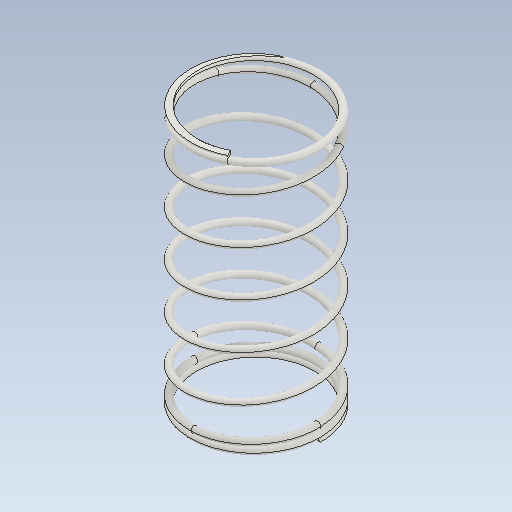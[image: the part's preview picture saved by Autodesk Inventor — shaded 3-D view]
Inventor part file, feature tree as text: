
AUTODESK INVENTOR PART (.ipt)
format: ipt  version: 2020 (Build 240168000, 168)  size: 788,480 bytes
history: native  units: mm
features: other x67, extrude x8, helix x5, sketch x3, sweep x2, plane x1
ambient origin geometry x8: Origin, YZ Plane, XZ Plane, XY Plane, X Axis, Y Axis, Z Axis, Center Point
bodies: Solid1 (feature_tree)
feature tree (86):
  other  "Main Coil Path(Right)"
  other  "Section Work Plane(Right)"
  other  "Start Work Plane(Right)"
  other  "End Work Plane(Right)"
  other  "End Cut Work Plane(Right)"
  other  "Start Cut Work Plane(Right)"
  other  "Plain Ends Cut Work Plane 1(Right)"
  other  "Plain Ends Cut Work Plane 2(Right)"
  sweep  "Main Coil Feature(R)"
  other  "Start Transition Coil 1(Right)"
  helix  "Coil  Start Transition 2(R)"  [1 undecoded]
  helix  "Coil  Start Transition 3(R)"  [1 undecoded]
  helix  "Coil  Start Transition 4(R)"  [1 undecoded]
  other  "Start Ends Coil(Right)"
  extrude  "Start Cut Feature(Right)"  Depth=10.0mm
  other  "End Transition Coil 1(Right)"
  other  "End Transition Coil 2(Right)"
  other  "End Transition Coil 3(Right)"
  other  "End Transition Coil 4(Right)"
  other  "End Coil(Right)"
  extrude  "End Cut Feature(Right)"  Depth=10.0mm
  extrude  "Plain Ends Cut Feature 1(Right)"  Depth=10.0mm
  extrude  "Plain Ends Cut  2(R)"  Depth=10.0mm TaperAngle=0.0deg
  other  "Main Coil Path(Left)"
  other  "Section Work Plane(Left)"
  other  "Start Work Plane(Left)"
  other  "End Work Plane(Left)"
  other  "End Cut Work Plane(Left)"
  other  "Start Cut Work Plane(Left)"
  other  "Plain Ends Cut Work Plane 1(Left)"
  other  "Plain Ends Cut Work Plane 2(Left)"
  sweep  "Main Coil Feature(L)"
  other  "Start Transition Coil 1(Left)"
  other  "Start Transition Coil 2(Left)"
  other  "Start Transition Coil 3(Left)"
  other  "Start Transition Coil 4(Left)"
  other  "Start Ends Coil(Left)"
  extrude  "Start Cut Feature(Left)"  Depth=10.0mm TaperAngle=0.0deg
  other  "End Transition Coil 1(Left)"
  other  "End Transition Coil 2(Left)"
  other  "End Transition Coil 3(Left)"
  other  "End Transition Coil 4(Left)"
  other  "End Coil(Left)"
  extrude  "End Cut Feature(Left)"  Depth=10.0mm
  extrude  "Cut Plain Ends Cut 1(L)"  TaperAngle=0.0deg  [1 undecoded]
  extrude  "Cut Plain Ends Cut 2(L)"  TaperAngle=0.0deg  [1 undecoded]
  other  "iMate Based Work Plane"
  other  "Preview Center Point"
  other  "Preview X Axis"
  other  "Path Section Sketch(Right)"
  other  "Srf1"
  helix  "Coil Section Sketch(Right)"  [1 undecoded]
  other  "Start Transition Coil Sketch 1(Right)"
  sketch  "Sketch  Start Transition 2(R)"  dims[d0=0.125mm d2=3.503747mm d3=10.0mm d4=45.745033mm]
  sketch  "Sketch  Start Transition 3(R)"  dims[d5=0.0mm d6=90.0deg d7=90.0deg d8=0.0mm d9=0.0mm d12=1.719816mm d13=-2.252275mm d14=0.5mm]
  sketch  "Sketch  Start Transition 4(R)"  dims[d15=0.0mm d16=2.75281mm d17=10.0mm d18=2.5mm d19=0.0mm d20=90.0deg d21=90.0deg d22=0.0mm d23=0.0mm d24=2.001874mm d25=10.0mm d26=2.5mm d27=0.0mm d28=90.0deg d29=90.0deg d30=0.0mm d31=0.0mm d32=1.250937mm d33=10.0mm d34=2.5mm d35=0.0mm d36=90.0deg d37=90.0deg d38=0.0mm d39=0.0mm d40=0.5mm d41=10.0mm d42=2.5mm d43=0.0mm d44=90.0deg d45=90.0deg d46=0.0mm d47=0.0mm d48=2.75281mm d49=10.0mm d50=1.875mm d51=0.0mm d52=90.0deg d53=90.0deg d54=0.0mm d55=0.0mm d56=2.001874mm d57=10.0mm d58=1.875mm d59=0.0mm d60=90.0deg d61=90.0deg d62=0.0mm d63=0.0mm d64=1.250937mm d65=10.0mm d66=1.875mm d67=0.0mm d68=90.0deg d69=90.0deg d70=0.0mm d71=0.0mm d72=0.5mm d73=10.0mm d74=1.875mm d75=0.0mm d76=90.0deg d77=90.0deg d78=0.0mm d79=0.0mm d81=10.0mm d82=15.0mm d83=0.0mm d84=90.0deg d85=90.0deg d86=0.0mm d87=0.0mm d88=0.503434mm d89=10.0mm d90=10.0mm d91=0.0mm d92=90.0deg d93=90.0deg d94=0.0mm d95=0.0mm d96=10.0mm d97=0.503434mm d98=0.0mm d99=10.0mm d100=0.503434mm d101=0.0mm d102=0.0mm d103=0.0mm d104=0.0mm d105=0.0mm d106=0.0mm d108=0.0mm d112=0.0mm d113=0.0mm d114=0.0mm d121=0.12928mm d131=0.0mm d132=0.0mm d133=0.0mm d134=0.0mm d135=0.125mm d137=3.503747mm d138=10.0mm d139=45.745033mm d140=0.0mm d141=90.0deg d142=90.0deg d143=0.0mm d144=0.0mm d145=1.719816mm d146=-2.252275mm d147=0.12928mm d148=0.003422mm d149=0.5mm d150=0.0mm d151=0.0mm d152=2.75281mm d153=10.0mm d154=2.5mm d155=0.0mm d156=90.0deg d157=90.0deg d158=0.0mm d159=0.0mm d160=2.001874mm d161=10.0mm d162=2.5mm d163=0.0mm d164=90.0deg d165=90.0deg d166=0.0mm d167=0.0mm d168=1.250937mm d169=10.0mm d170=2.5mm d171=0.0mm d172=90.0deg d173=90.0deg d174=0.0mm d175=0.0mm d176=0.5mm d177=10.0mm d178=2.5mm d179=0.0mm d180=90.0deg d181=90.0deg d182=0.0mm d183=0.0mm d184=10.0mm d185=10.0mm d186=10.0mm d187=10.0mm d188=0.503434mm d189=10.0mm d190=15.0mm d191=0.0mm d192=90.0deg d193=90.0deg d194=0.0mm d195=0.0mm d196=10.0mm d197=10.0mm d198=0.503434mm d199=0.0mm d200=10.0mm d201=2.75281mm d202=10.0mm d203=1.875mm d204=0.0mm d205=90.0deg d206=90.0deg d207=0.0mm d208=0.0mm d209=10.0mm d210=2.001874mm d211=10.0mm d212=1.875mm d213=0.0mm d214=90.0deg d215=90.0deg d216=0.0mm d217=0.0mm d218=1.250937mm d219=10.0mm d220=1.875mm d221=0.0mm d222=90.0deg d223=90.0deg d224=0.0mm d225=0.0mm d226=0.5mm d227=10.0mm d228=1.875mm d229=0.0mm d230=90.0deg d231=90.0deg d232=0.0mm d233=0.0mm d234=10.0mm d235=10.0mm d236=10.0mm d237=0.503434mm d238=10.0mm d239=10.0mm d240=0.0mm d241=90.0deg d242=90.0deg d243=0.0mm d244=0.0mm d245=10.0mm d246=0.503434mm d247=0.0mm d248=10.0mm d249=10.0mm d254=10.0mm d255=10.0mm d256=0.0mm d257=20.0mm d258=-0.003422mm d259=10.0mm d260=10.0mm d261=0.0mm d262=10.0mm d263=10.0mm d264=10.0mm d265=0.0mm d266=10.0mm d267=0.0mm d270=-2.189775mm d271=0.0mm d272=10.0mm d273=10.0mm d274=0.0mm d275=20.0mm d276=-157.079633mm d277=9.5mm d278=9.5mm d279=0.0mm d280=0.0mm]
  other  "End Transition Coil Sketch 1(Right)"
  other  "End Transition Coil Sketch 2(Right)"
  other  "End Transition Coil Sketch 3(Right)"
  other  "End Transition Coil Sketch 4(Right)"
  other  "Start Ends Skecth(Right)"
  other  "End Coil Skecth(Right)"
  other  "End Cut Sketch(Right)"
  other  "Start Cut Sketch(Right)"
  other  "Path Section Sketch(Left)"
  other  "Srf2"
  helix  "Coil Section Sketch(Left)"  [1 undecoded]
  other  "Start Transition Coil Sketch 1(Left)"
  other  "Start Transition Coil Sketch 2(Left)"
  other  "Start Transition Coil Sketch 3(Left)"
  other  "Start Transition Coil Sketch 4(Left)"
  other  "Start Ends Skecth(Left)"
  other  "Start Cut Sketch(Left)"
  other  "End Transition Coil Sketch 1(Left)"
  other  "End Transition Coil Sketch 2(Left)"
  other  "End Transition Coil Sketch 3(Left)"
  other  "End Transition Coil Sketch 4(Left)"
  other  "End Coil Skecth(Left)"
  other  "End Cut Sketch(Left)"
  other  "Plain Ends Cut Sketch 2(Left)"
  other  "Plain Ends Cut Sketch 2(Right)"
  other  "Plain Ends Cut Sketch 1(Right)"
  other  "Plain Ends Cut Sketch 1(Left)"
  plane  "Work Plane Start Section"
  other  "Basic Curve(Right)"
  other  "Basic Curve(Left)"
note: 7 required parameter values undecoded (feature->parameter linkage not recoverable at this tier; creation-order binding heuristic only, values carry confidence <= 0.55)
